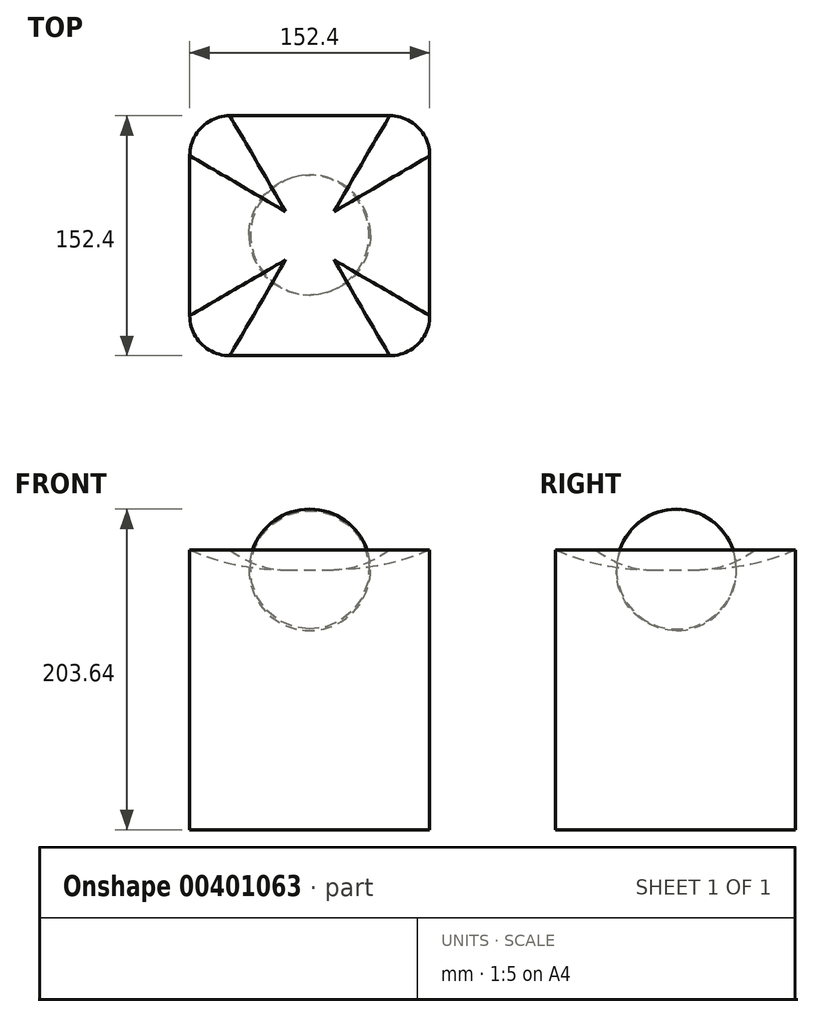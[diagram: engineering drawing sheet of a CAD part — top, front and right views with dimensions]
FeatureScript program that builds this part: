
annotation { "Feature Type Name" : "Feature", "Feature Type Description" : "" }
export const myFeature = defineFeature(function(context is Context, id is Id, definition is map)
    precondition{}
    {
        {
            var Q0;
            Q0=qCreatedBy(makeId("Top.planeOp"),FACE);
            var sketch = newSketch(context, id + "F0", { "sketchPlane" : qUnion([Q0])});
            skLineSegment(sketch, "E0.bottom", {"start": v(-101.6, 101.6) * mm, "end": v(101.6, 101.6) * mm});
            skLineSegment(sketch, "E0.top", {"start": v(-101.6, -101.6) * mm, "end": v(101.6, -101.6) * mm});
            skLineSegment(sketch, "E0.left", {"start": v(-101.6, 101.6) * mm, "end": v(-101.6, -101.6) * mm});
            skLineSegment(sketch, "E0.right", {"start": v(101.6, 101.6) * mm, "end": v(101.6, -101.6) * mm});
            skSolve(sketch);
        }
        {
            var Q0;
            Q0=makeQuery(id+"F0.imprint","IMPRINT",FACE,{"disambiguationData":[TD([[makeQuery(id+"F0.imprint","IMPRINT",EDGE,{"derivedFrom":sQuery(id+"F0.wireOp",EDGE,"E0.bottom")}),-1.0]])]});
            extrude(context, id + "F1", {"entities" : qUnion([Q0]), "depth" : 177.8 * mm});
        }
        {
            var Q0;
            Q0=makeQuery(id+"F1.opExtrude","CAP_FACE",FACE,{"disambiguationData":[OSD([sQuery(id+"F0.wireOp",EDGE,"E0.bottom"),sQuery(id+"F0.wireOp",EDGE,"E0.top"),sQuery(id+"F0.wireOp",EDGE,"E0.left"),sQuery(id+"F0.wireOp",EDGE,"E0.right")])],"isStart":false});
            var Q1;
            Q1=makeQuery(id+"F1.opExtrude","SWEPT_FACE",FACE,{"disambiguationData":[OSD([sQuery(id+"F0.wireOp",EDGE,"E0.top")])]});
            var Q2;
            Q2=makeQuery(id+"F1.opExtrude","SWEPT_FACE",FACE,{"disambiguationData":[OSD([sQuery(id+"F0.wireOp",EDGE,"E0.left")])]});
            var Q3;
            Q3=makeQuery(id+"F1.opExtrude","SWEPT_FACE",FACE,{"disambiguationData":[OSD([sQuery(id+"F0.wireOp",EDGE,"E0.bottom")])]});
            var Q4;
            Q4=makeQuery(id+"F1.opExtrude","SWEPT_FACE",FACE,{"disambiguationData":[OSD([sQuery(id+"F0.wireOp",EDGE,"E0.right")])]});
            var Q5;
            Q5=makeQuery(id+"F1.opExtrude","CAP_FACE",FACE,{"disambiguationData":[OSD([sQuery(id+"F0.wireOp",EDGE,"E0.bottom"),sQuery(id+"F0.wireOp",EDGE,"E0.top"),sQuery(id+"F0.wireOp",EDGE,"E0.left"),sQuery(id+"F0.wireOp",EDGE,"E0.right")])],"isStart":true});
            fillet(context, id + "F2", {"entities" : qUnion([Q0, Q1, Q2, Q3, Q4, Q5]), "radius" : 25.4 * mm, "tangentPropagation" : true, "allowEdgeOverflow" : false});
        }
        {
            var Q0;
            Q0=makeQuery(id+"F1.opExtrude","CAP_FACE",FACE,{"disambiguationData":[OSD([sQuery(id+"F0.wireOp",EDGE,"E0.bottom"),sQuery(id+"F0.wireOp",EDGE,"E0.top"),sQuery(id+"F0.wireOp",EDGE,"E0.left"),sQuery(id+"F0.wireOp",EDGE,"E0.right")])],"isStart":false});
            var sketch = newSketch(context, id + "F3", { "sketchPlane" : qUnion([Q0])});
            skLineSegment(sketch, "E1.0", {"start": v(-25.4, -25.4) * mm, "end": v(25.4, -25.4) * mm});
            skLineSegment(sketch, "E1.1", {"start": v(-25.4, 25.4) * mm, "end": v(-25.4, -25.4) * mm});
            skLineSegment(sketch, "E1.2", {"start": v(25.4, 25.4) * mm, "end": v(-25.4, 25.4) * mm});
            skLineSegment(sketch, "E1.3", {"start": v(25.4, -25.4) * mm, "end": v(25.4, 25.4) * mm});
            skLineSegment(sketch, "E2.bottom", {"start": v(-50.8, 76.2) * mm, "end": v(50.8, 76.2) * mm});
            skLineSegment(sketch, "E2.top", {"start": v(-50.8, -76.2) * mm, "end": v(50.8, -76.2) * mm});
            skLineSegment(sketch, "E2.left", {"start": v(-76.2, 50.8) * mm, "end": v(-76.2, -50.8) * mm});
            skLineSegment(sketch, "E2.right", {"start": v(76.2, 50.8) * mm, "end": v(76.2, -50.8) * mm});
            skPoint(sketch, "E3.visualSharp", {"position": v(-76.2, 76.2) * mm});
            skArc(sketch, "E3.filletArc", {"start": v(-50.8, 76.2) * mm, "mid": v(-68.76, 68.76) * mm, "end": v(-76.2, 50.8) * mm});
            skPoint(sketch, "E4.visualSharp", {"position": v(-76.2, -76.2) * mm});
            skArc(sketch, "E4.filletArc", {"start": v(-76.2, -50.8) * mm, "mid": v(-68.76, -68.76) * mm, "end": v(-50.8, -76.2) * mm});
            skPoint(sketch, "E5.visualSharp", {"position": v(76.2, -76.2) * mm});
            skArc(sketch, "E5.filletArc", {"start": v(50.8, -76.2) * mm, "mid": v(68.76, -68.76) * mm, "end": v(76.2, -50.8) * mm});
            skPoint(sketch, "E6.visualSharp", {"position": v(76.2, 76.2) * mm});
            skArc(sketch, "E6.filletArc", {"start": v(76.2, 50.8) * mm, "mid": v(68.76, 68.76) * mm, "end": v(50.8, 76.2) * mm});
            skSolve(sketch);
        }
        {
            var Q0;
            Q0=makeQuery(id+"F3.imprint","IMPRINT",FACE,{"disambiguationData":[TD([[makeQuery(id+"F3.imprint","IMPRINT",EDGE,{"derivedFrom":sQuery(id+"F3.wireOp",EDGE,"E1.0")}),-1.0]])]});
            extrude(context, id + "F4", {"entities" : qUnion([Q0]), "operationType" : NewBodyOperationType.REMOVE, "oppositeDirection" : true, "depth" : 12.7 * mm});
        }
        {
            var Q0;
            Q0=makeQuery(id+"F1.opExtrude","CAP_FACE",FACE,{"disambiguationData":[OSD([sQuery(id+"F0.wireOp",EDGE,"E0.bottom"),sQuery(id+"F0.wireOp",EDGE,"E0.top"),sQuery(id+"F0.wireOp",EDGE,"E0.left"),sQuery(id+"F0.wireOp",EDGE,"E0.right")])],"isStart":false});
            var sketch = newSketch(context, id + "F5", { "sketchPlane" : qUnion([Q0])});
            skCircle(sketch, "E7", {"center": v(0, 0) * mm, "radius": 35.92 * mm});
            skSolve(sketch);
        }
        {
            var Q0;
            {var subQ1=makeQuery(id+"F4.boolean.opBoolean","COPY",EDGE,{"derivedFrom":makeQuery(id+"F4.opExtrude","CAP_EDGE",EDGE,{"disambiguationData":[OSD([sQuery(id+"F3.wireOp",EDGE,"E1.2")])],"isStart":true})});Q0=makeQuery(id+"F5.imprint","IMPRINT",FACE,{"disambiguationData":[TD([[makeQuery(id+"F5.imprint","IMPRINT",EDGE,{"derivedFrom":subQ1}),-1.0]])]});}
            var Q1;
            {var subQ1=makeQuery(id+"F4.boolean.opBoolean","COPY",EDGE,{"derivedFrom":makeQuery(id+"F4.opExtrude","CAP_EDGE",EDGE,{"disambiguationData":[OSD([sQuery(id+"F3.wireOp",EDGE,"E1.1")])],"isStart":true})});Q1=makeQuery(id+"F5.imprint","IMPRINT",FACE,{"disambiguationData":[TD([[makeQuery(id+"F5.imprint","IMPRINT",EDGE,{"derivedFrom":subQ1}),-1.0]])]});}
            var Q2;
            {var subQ1=makeQuery(id+"F4.boolean.opBoolean","COPY",EDGE,{"derivedFrom":makeQuery(id+"F4.opExtrude","CAP_EDGE",EDGE,{"disambiguationData":[OSD([sQuery(id+"F3.wireOp",EDGE,"E1.0")])],"isStart":true})});Q2=makeQuery(id+"F5.imprint","IMPRINT",FACE,{"disambiguationData":[TD([[makeQuery(id+"F5.imprint","IMPRINT",EDGE,{"derivedFrom":subQ1}),-1.0]])]});}
            var Q3;
            Q3=makeQuery(id+"F5.imprint","IMPRINT",FACE,{"disambiguationData":[TD([[makeQuery(id+"F5.imprint","IMPRINT",EDGE,{"derivedFrom":makeQuery(id+"F4.boolean.opBoolean","COPY",EDGE,{"derivedFrom":makeQuery(id+"F4.opExtrude","CAP_EDGE",EDGE,{"disambiguationData":[OSD([sQuery(id+"F3.wireOp",EDGE,"E1.0")])],"isStart":true})})}),1.0]])]});
            var Q4;
            {var subQ1=makeQuery(id+"F4.boolean.opBoolean","COPY",EDGE,{"derivedFrom":makeQuery(id+"F4.opExtrude","CAP_EDGE",EDGE,{"disambiguationData":[OSD([sQuery(id+"F3.wireOp",EDGE,"E1.3")])],"isStart":true})});Q4=makeQuery(id+"F5.imprint","IMPRINT",FACE,{"disambiguationData":[TD([[makeQuery(id+"F5.imprint","IMPRINT",EDGE,{"derivedFrom":subQ1}),-1.0]])]});}
            extrude(context, id + "F6", {"entities" : qUnion([Q0, Q1, Q2, Q3, Q4]), "operationType" : NewBodyOperationType.REMOVE, "oppositeDirection" : true, "depth" : 12.7 * mm});
        }
        {
            var Q0;
            Q0=makeQuery(id+"F6.boolean.opBoolean","MERGE",FACE,{"derivedFrom":[makeQuery(id+"F4.boolean.opBoolean","COPY",FACE,{"derivedFrom":makeQuery(id+"F4.opExtrude","CAP_FACE",FACE,{"disambiguationData":[OSD([sQuery(id+"F0.wireOp",EDGE,"E0.bottom"),sQuery(id+"F0.wireOp",EDGE,"E0.top"),sQuery(id+"F0.wireOp",EDGE,"E0.left"),sQuery(id+"F0.wireOp",EDGE,"E0.right"),sQuery(id+"F3.wireOp",EDGE,"E1.0"),sQuery(id+"F3.wireOp",EDGE,"E1.1"),sQuery(id+"F3.wireOp",EDGE,"E1.2"),sQuery(id+"F3.wireOp",EDGE,"E1.3")])],"isStart":false})}),makeQuery(id+"F6.opExtrude","CAP_FACE",FACE,{"disambiguationData":[OSD([sQuery(id+"F5.wireOp",EDGE,"E7")])],"isStart":false})]});
            fillet(context, id + "F7", {"entities" : qUnion([Q0]), "radius" : 152.4 * mm, "tangentPropagation" : true, "allowEdgeOverflow" : false});
        }
        {
            var Q0;
            Q0=makeQuery(id+"F6.boolean.opBoolean","MERGE",FACE,{"derivedFrom":[makeQuery(id+"F4.boolean.opBoolean","COPY",FACE,{"derivedFrom":makeQuery(id+"F4.opExtrude","CAP_FACE",FACE,{"disambiguationData":[OSD([sQuery(id+"F3.wireOp",EDGE,"E1.0"),sQuery(id+"F3.wireOp",EDGE,"E1.1"),sQuery(id+"F3.wireOp",EDGE,"E1.2"),sQuery(id+"F3.wireOp",EDGE,"E1.3"),sQuery(id+"F3.wireOp",EDGE,"E2.bottom"),sQuery(id+"F3.wireOp",EDGE,"E2.top"),sQuery(id+"F3.wireOp",EDGE,"E2.left"),sQuery(id+"F3.wireOp",EDGE,"E2.right"),sQuery(id+"F3.wireOp",EDGE,"E3.filletArc"),sQuery(id+"F3.wireOp",EDGE,"E4.filletArc"),sQuery(id+"F3.wireOp",EDGE,"E5.filletArc"),sQuery(id+"F3.wireOp",EDGE,"E6.filletArc")])],"isStart":false})}),makeQuery(id+"F6.opExtrude","CAP_FACE",FACE,{"disambiguationData":[OSD([sQuery(id+"F5.wireOp",EDGE,"E7")])],"isStart":false})]});
            cPlane(context, id + "F8", {"entities" : qUnion([Q0]), "cplaneType" : CPlaneType.OFFSET, "offset" : 25.4 * mm, "oppositeDirection" : true, "width" : 152.4 * mm, "height" : 152.4 * mm});
        }
        {
            var Q0;
            Q0=qCreatedBy(id+"F8.planeOp",FACE);
            var sketch = newSketch(context, id + "F9", { "sketchPlane" : qUnion([Q0])});
            skArc(sketch, "E8", {"start": v(0, 38.1) * mm, "mid": v(-38.1, 0) * mm, "end": v(0, -38.1) * mm});
            skLineSegment(sketch, "E9", {"start": v(0, 38.1) * mm, "end": v(0, -38.1) * mm});
            skSolve(sketch);
        }
        {
            var Q0;
            Q0=makeQuery(id+"F6.boolean.opBoolean","MERGE",FACE,{"derivedFrom":[makeQuery(id+"F4.boolean.opBoolean","COPY",FACE,{"derivedFrom":makeQuery(id+"F4.opExtrude","CAP_FACE",FACE,{"disambiguationData":[OSD([sQuery(id+"F3.wireOp",EDGE,"E1.0"),sQuery(id+"F3.wireOp",EDGE,"E1.1"),sQuery(id+"F3.wireOp",EDGE,"E1.2"),sQuery(id+"F3.wireOp",EDGE,"E1.3"),sQuery(id+"F3.wireOp",EDGE,"E2.bottom"),sQuery(id+"F3.wireOp",EDGE,"E2.top"),sQuery(id+"F3.wireOp",EDGE,"E2.left"),sQuery(id+"F3.wireOp",EDGE,"E2.right"),sQuery(id+"F3.wireOp",EDGE,"E3.filletArc"),sQuery(id+"F3.wireOp",EDGE,"E4.filletArc"),sQuery(id+"F3.wireOp",EDGE,"E5.filletArc"),sQuery(id+"F3.wireOp",EDGE,"E6.filletArc")])],"isStart":false})}),makeQuery(id+"F6.opExtrude","CAP_FACE",FACE,{"disambiguationData":[OSD([sQuery(id+"F5.wireOp",EDGE,"E7")])],"isStart":false})]});
            var sketch = newSketch(context, id + "F10", { "sketchPlane" : qUnion([Q0])});
            skSolve(sketch);
        }
        {
            var Q0;
            {var subQ0=sQuery(id+"F0.wireOp",EDGE,"E0.right");var subQ1=sQuery(id+"F0.wireOp",EDGE,"E0.bottom");Q0=makeQuery(id+"F4.boolean.opBoolean","SPLIT",FACE,{"disambiguationData":[TD([makeQuery(id+"F4.opExtrude","SWEPT_FACE",FACE,{"disambiguationData":[OSD([sQuery(id+"F3.wireOp",EDGE,"E6.filletArc")])]})])],"derivedFrom":makeQuery(id+"F1.opExtrude","CAP_FACE",FACE,{"disambiguationData":[OSD([subQ1,sQuery(id+"F0.wireOp",EDGE,"E0.top"),sQuery(id+"F0.wireOp",EDGE,"E0.left"),subQ0])],"isStart":false})});}
            cPlane(context, id + "F11", {"entities" : qUnion([Q0]), "cplaneType" : CPlaneType.OFFSET, "offset" : 25.4 * mm, "width" : 152.4 * mm, "height" : 152.4 * mm});
        }
        {
            var Q0;
            Q0=qCreatedBy(id+"F11.planeOp",FACE);
            var sketch = newSketch(context, id + "F12", { "sketchPlane" : qUnion([Q0])});
            skLineSegment(sketch, "E10.bottom", {"start": v(-50.8, 76.2) * mm, "end": v(50.8, 76.2) * mm});
            skLineSegment(sketch, "E10.top", {"start": v(-50.8, -76.2) * mm, "end": v(50.8, -76.2) * mm});
            skLineSegment(sketch, "E10.left", {"start": v(-76.2, 50.8) * mm, "end": v(-76.2, -50.8) * mm});
            skLineSegment(sketch, "E10.right", {"start": v(76.2, 50.8) * mm, "end": v(76.2, -50.8) * mm});
            skPoint(sketch, "E11.visualSharp", {"position": v(-76.2, 76.2) * mm});
            skArc(sketch, "E11.filletArc", {"start": v(-50.8, 76.2) * mm, "mid": v(-68.76, 68.76) * mm, "end": v(-76.2, 50.8) * mm});
            skPoint(sketch, "E12.visualSharp", {"position": v(-76.2, -76.2) * mm});
            skArc(sketch, "E12.filletArc", {"start": v(-76.2, -50.8) * mm, "mid": v(-68.76, -68.76) * mm, "end": v(-50.8, -76.2) * mm});
            skPoint(sketch, "E13.visualSharp", {"position": v(76.2, -76.2) * mm});
            skArc(sketch, "E13.filletArc", {"start": v(50.8, -76.2) * mm, "mid": v(68.76, -68.76) * mm, "end": v(76.2, -50.8) * mm});
            skPoint(sketch, "E14.visualSharp", {"position": v(76.2, 76.2) * mm});
            skArc(sketch, "E14.filletArc", {"start": v(76.2, 50.8) * mm, "mid": v(68.76, 68.76) * mm, "end": v(50.8, 76.2) * mm});
            skLineSegment(sketch, "E15.0", {"start": v(-50.8, 127) * mm, "end": v(50.8, 127) * mm});
            skArc(sketch, "E15.1", {"start": v(127, 50.8) * mm, "mid": v(104.68, 104.68) * mm, "end": v(50.8, 127) * mm});
            skArc(sketch, "E15.2", {"start": v(-50.8, 127) * mm, "mid": v(-104.68, 104.68) * mm, "end": v(-127, 50.8) * mm});
            skLineSegment(sketch, "E15.3", {"start": v(127, 50.8) * mm, "end": v(127, -50.8) * mm});
            skLineSegment(sketch, "E15.4", {"start": v(-127, 50.8) * mm, "end": v(-127, -50.8) * mm});
            skArc(sketch, "E15.5", {"start": v(-127, -50.8) * mm, "mid": v(-104.68, -104.68) * mm, "end": v(-50.8, -127) * mm});
            skLineSegment(sketch, "E15.6", {"start": v(-50.8, -127) * mm, "end": v(50.8, -127) * mm});
            skArc(sketch, "E15.7", {"start": v(50.8, -127) * mm, "mid": v(104.68, -104.68) * mm, "end": v(127, -50.8) * mm});
            skSolve(sketch);
        }
        {
            var Q0;
            Q0=makeQuery(id+"F12.imprint","IMPRINT",FACE,{"disambiguationData":[TD([[makeQuery(id+"F12.imprint","IMPRINT",EDGE,{"derivedFrom":sQuery(id+"F12.wireOp",EDGE,"E10.bottom")}),1.0]])]});
            extrude(context, id + "F13", {"entities" : qUnion([Q0]), "operationType" : NewBodyOperationType.REMOVE, "oppositeDirection" : true, "depth" : 1803.4 * mm});
        }
        {
            var Q0;
            {var subQ0=sQuery(id+"F3.wireOp",EDGE,"E2.right");var subQ1=sQuery(id+"F3.wireOp",EDGE,"E2.left");var subQ2=sQuery(id+"F3.wireOp",EDGE,"E2.top");var subQ3=sQuery(id+"F3.wireOp",EDGE,"E2.bottom");var subQ4=makeQuery(id+"F6.boolean.opBoolean","MERGE",FACE,{"derivedFrom":[makeQuery(id+"F4.boolean.opBoolean","COPY",FACE,{"derivedFrom":makeQuery(id+"F4.opExtrude","CAP_FACE",FACE,{"disambiguationData":[OSD([sQuery(id+"F3.wireOp",EDGE,"E1.0"),sQuery(id+"F3.wireOp",EDGE,"E1.1"),sQuery(id+"F3.wireOp",EDGE,"E1.2"),sQuery(id+"F3.wireOp",EDGE,"E1.3"),subQ3,subQ2,subQ1,subQ0,sQuery(id+"F3.wireOp",EDGE,"E3.filletArc"),sQuery(id+"F3.wireOp",EDGE,"E4.filletArc"),sQuery(id+"F3.wireOp",EDGE,"E5.filletArc"),sQuery(id+"F3.wireOp",EDGE,"E6.filletArc")])],"isStart":false})}),makeQuery(id+"F6.opExtrude","CAP_FACE",FACE,{"disambiguationData":[OSD([sQuery(id+"F5.wireOp",EDGE,"E7")])],"isStart":false})]});Q0=makeQuery(id+"F10.imprint","IMPRINT",FACE,{"disambiguationData":[TD([[makeQuery(id+"F10.imprint","IMPRINT",EDGE,{"derivedFrom":makeQuery(id+"F7.opFillet","BLEND_EDGE",EDGE,{"blendedFrom":[makeQuery(id+"F4.boolean.opBoolean","COPY",EDGE,{"derivedFrom":makeQuery(id+"F4.opExtrude","CAP_EDGE",EDGE,{"disambiguationData":[OSD([subQ3])],"isStart":false})}),subQ4],"blendedInto":[subQ4]})}),1.0]])]});}
            var sketch = newSketch(context, id + "F14", { "sketchPlane" : qUnion([Q0])});
            skArc(sketch, "E16", {"start": v(0, 38.59) * mm, "mid": v(-37.66, 0.49) * mm, "end": v(0, -37.6) * mm});
            skLineSegment(sketch, "E17", {"start": v(0, 38.59) * mm, "end": v(0, -37.6) * mm});
            skSolve(sketch);
        }
        {
            var Q0;
            Q0 = qSketchRegion(id + "F14", true);
            var Q1;
            Q1=sQuery(id+"F14.wireOp",EDGE,"E17");
            revolve(context, id + "F15", {"entities" : qUnion([Q0]), "axis" : qUnion([Q1]), "revolveType" : RevolveType.FULL});
        }
    });
